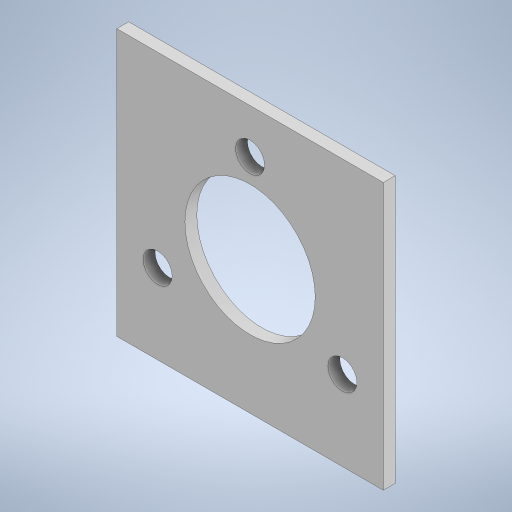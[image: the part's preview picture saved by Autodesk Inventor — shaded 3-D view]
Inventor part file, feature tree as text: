
AUTODESK INVENTOR PART (.ipt)
format: ipt  version: 2024 (Build 280153000, 153)  size: 237,568 bytes
history: native  units: in
note: dims shown in document units (in); Inventor stores cm internally (conversion verified against a paired STEP export)
features: extrude x1, sketch x1
ambient origin geometry x8: Origin, YZ Plane, XZ Plane, XY Plane, X Axis, Y Axis, Z Axis, Center Point
bodies: Body1 (feature_tree)
feature tree (2):
  extrude  "Extrusion2"  Depth=1.7717in
  sketch  "Sketch1"  dims[d0=1.7717in d1=1.7717in d2=0.8661in d3=0.5906in d4=0.6142in d5=120.0deg d6=0.6142in d7=120.0deg d8=0.1929in d9=0.1929in d10=0.1929in d16=0.0787in d17=0.0in d11=0.0197in d12=0.0344in d13=0.0197in d14=0.0344in]
